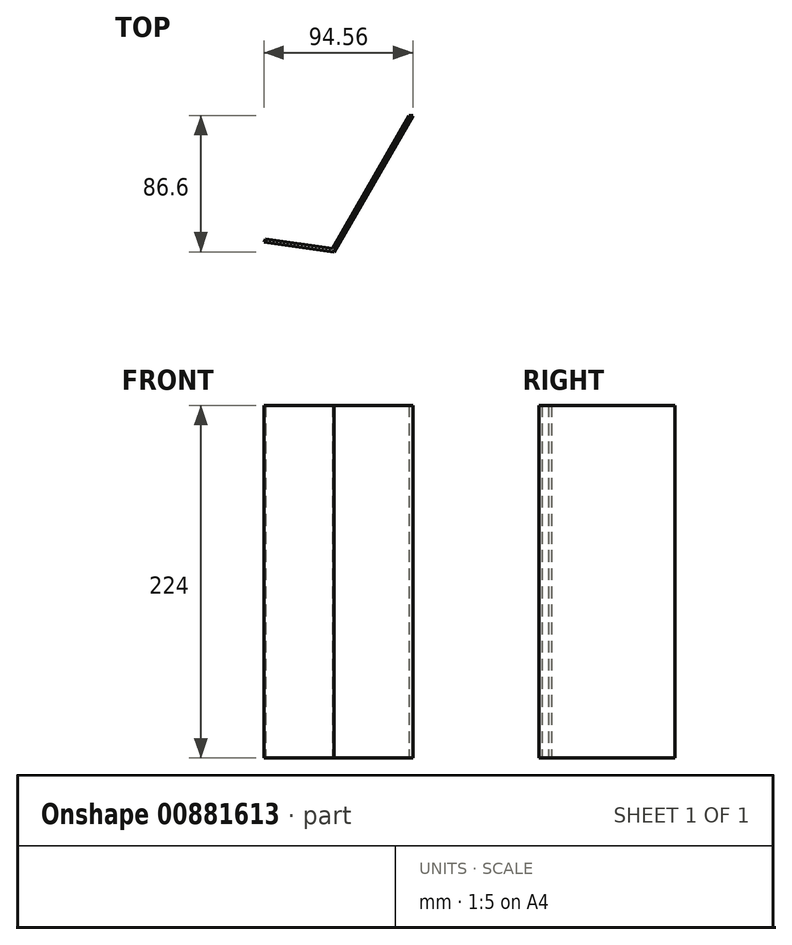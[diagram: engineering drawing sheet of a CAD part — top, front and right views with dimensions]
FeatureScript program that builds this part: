
annotation { "Feature Type Name" : "Feature", "Feature Type Description" : "" }
export const myFeature = defineFeature(function(context is Context, id is Id, definition is map)
    precondition{}
    {
        {
            var Q0;
            Q0=qCreatedBy(makeId("Top.planeOp"),FACE);
            var sketch = newSketch(context, id + "F0", { "sketchPlane" : qUnion([Q0])});
            skPoint(sketch, "E0", {"position": v(72.97, 86.6) * mm});
            skPoint(sketch, "E1", {"position": v(22.97, 0) * mm});
            skPoint(sketch, "E2", {"position": v(21.91, 2.17) * mm});
            skPoint(sketch, "E3", {"position": v(70.66, 86.6) * mm});
            skLineSegment(sketch, "E4", {"start": v(70.66, 86.6) * mm, "end": v(72.97, 86.6) * mm});
            skLineSegment(sketch, "E5", {"start": v(72.97, 86.6) * mm, "end": v(22.97, 0) * mm});
            skLineSegment(sketch, "E6", {"start": v(22.97, 0) * mm, "end": v(-21.59, 6.26) * mm});
            skLineSegment(sketch, "E7", {"start": v(-20.51, 8.13) * mm, "end": v(21.91, 2.17) * mm});
            skLineSegment(sketch, "E8", {"start": v(21.91, 2.17) * mm, "end": v(70.66, 86.6) * mm});
            skLineSegment(sketch, "E9", {"start": v(-21.59, 6.26) * mm, "end": v(-20.51, 8.13) * mm});
            skSolve(sketch);
        }
        {
            var Q0;
            Q0 = qSketchRegion(id + "F0", true);
            extrude(context, id + "F1", {"entities" : qUnion([Q0]), "depth" : 224 * mm, "offsetDistance" : 25 * mm});
        }
    });
